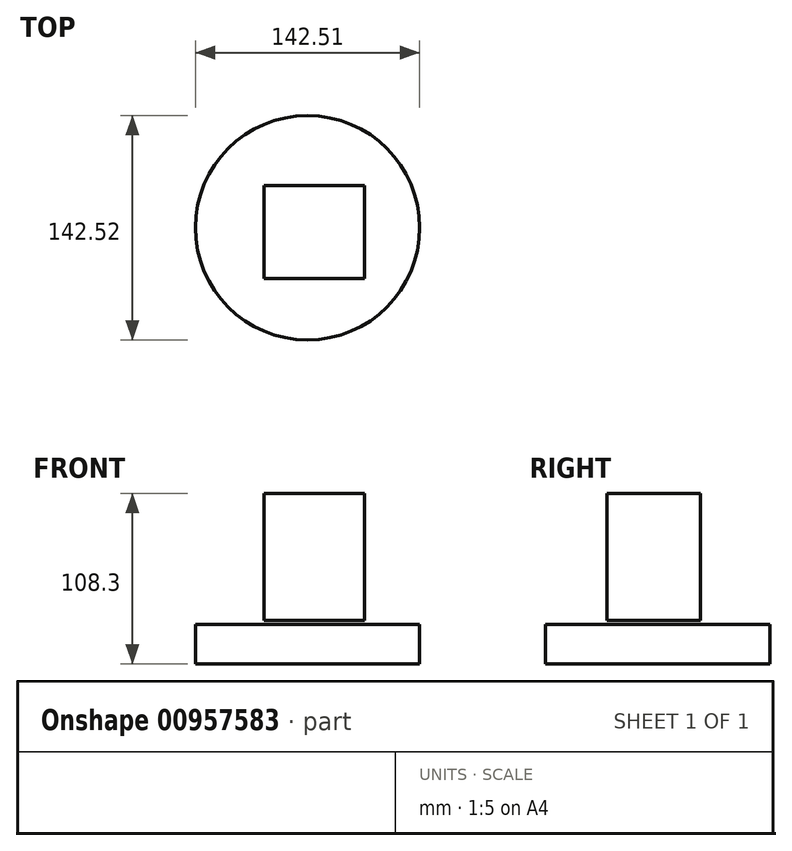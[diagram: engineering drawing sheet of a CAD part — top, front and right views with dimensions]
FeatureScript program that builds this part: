
annotation { "Feature Type Name" : "Feature", "Feature Type Description" : "" }
export const myFeature = defineFeature(function(context is Context, id is Id, definition is map)
    precondition{}
    {
        {
            var Q0;
            Q0=qCreatedBy(makeId("Front.planeOp"),FACE);
            var sketch = newSketch(context, id + "F0", { "sketchPlane" : qUnion([Q0])});
            skLineSegment(sketch, "E0.bottom", {"start": v(0, 83.3) * mm, "end": v(63.94, 83.3) * mm});
            skLineSegment(sketch, "E0.top", {"start": v(0, 27.53) * mm, "end": v(63.94, 27.53) * mm});
            skLineSegment(sketch, "E0.left", {"start": v(0, 83.3) * mm, "end": v(0, 27.53) * mm});
            skLineSegment(sketch, "E0.right", {"start": v(63.94, 83.3) * mm, "end": v(63.94, 27.53) * mm});
            skSolve(sketch);
        }
        {
            var Q0;
            Q0=makeQuery(id+"F0.imprint","IMPRINT",FACE,{"disambiguationData":[TD([[makeQuery(id+"F0.imprint","IMPRINT",EDGE,{"derivedFrom":sQuery(id+"F0.wireOp",EDGE,"E0.bottom")}),-1.0]])]});
            extrude(context, id + "F1", {"entities" : qUnion([Q0]), "depth" : 59.2 * mm, "offsetDistance" : 25 * mm});
        }
        {
            var Q0;
            Q0=qCreatedBy(makeId("Top.planeOp"),FACE);
            var sketch = newSketch(context, id + "F2", { "sketchPlane" : qUnion([Q0])});
            skCircle(sketch, "E1", {"center": v(27.68, -26.96) * mm, "radius": 71.26 * mm});
            skSolve(sketch);
        }
        {
            var Q0;
            Q0=makeQuery(id+"F2.imprint","IMPRINT",FACE,{"disambiguationData":[TD([[makeQuery(id+"F2.imprint","IMPRINT",EDGE,{"derivedFrom":sQuery(id+"F2.wireOp",EDGE,"E1")}),1.0]])]});
            extrude(context, id + "F3", {"entities" : qUnion([Q0]), "oppositeDirection" : true, "depth" : 25 * mm, "offsetDistance" : 25 * mm});
        }
        {
            var Q0;
            Q0=makeQuery(id+"F1.opExtrude","SWEPT_FACE",FACE,{"disambiguationData":[OSD([sQuery(id+"F0.wireOp",EDGE,"E0.top")])]});
            extrude(context, id + "F4", {"entities" : qUnion([Q0]), "operationType" : NewBodyOperationType.ADD, "depth" : 25 * mm, "offsetDistance" : 25 * mm});
        }
    });
